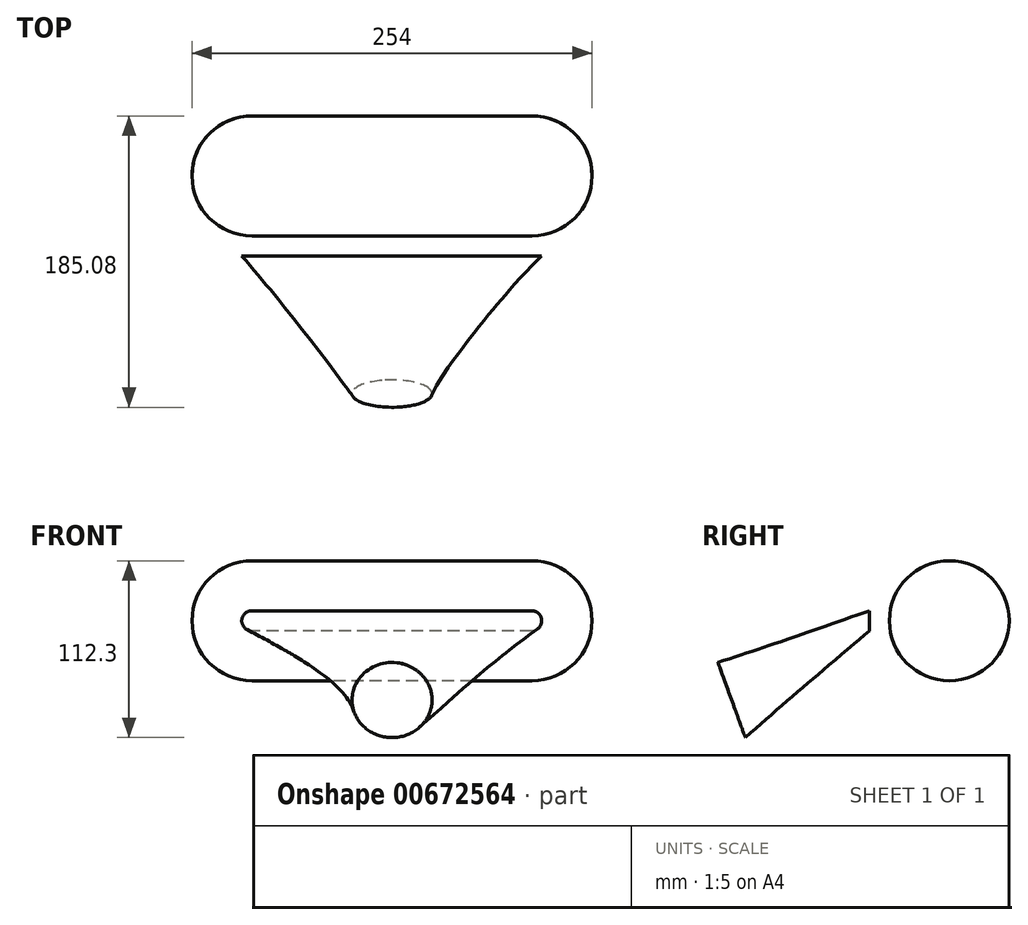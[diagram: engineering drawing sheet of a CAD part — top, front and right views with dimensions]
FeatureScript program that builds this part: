
annotation { "Feature Type Name" : "Feature", "Feature Type Description" : "" }
export const myFeature = defineFeature(function(context is Context, id is Id, definition is map)
    precondition{}
    {
        {
            var Q0;
            Q0=qCreatedBy(makeId("Top.planeOp"),FACE);
            var sketch = newSketch(context, id + "F0", { "sketchPlane" : qUnion([Q0])});
            skLineSegment(sketch, "E0", {"start": v(-127, 0) * mm, "end": v(127, 0) * mm});
            skArc(sketch, "E1", {"start": v(-127, 0) * mm, "mid": v(-115.84, 26.94) * mm, "end": v(-88.9, 38.1) * mm});
            skArc(sketch, "E2", {"start": v(127, 0) * mm, "mid": v(115.84, 26.94) * mm, "end": v(88.9, 38.1) * mm});
            skLineSegment(sketch, "E3", {"start": v(-88.9, 38.1) * mm, "end": v(88.9, 38.1) * mm});
            skSolve(sketch);
        }
        {
            var Q0;
            Q0=makeQuery(id+"F0.imprint","IMPRINT",FACE,{"disambiguationData":[TD([[makeQuery(id+"F0.imprint","IMPRINT",EDGE,{"derivedFrom":sQuery(id+"F0.wireOp",EDGE,"E0")}),1.0]])]});
            var Q1;
            Q1=sQuery(id+"F0.wireOp",EDGE,"E0");
            revolve(context, id + "F1", {"entities" : qUnion([Q0]), "axis" : qUnion([Q1]), "revolveType" : RevolveType.FULL});
        }
        {
            var Q0;
            Q0=qCreatedBy(makeId("Front.planeOp"),FACE);
            cPlane(context, id + "F2", {"entities" : qUnion([Q0]), "cplaneType" : CPlaneType.OFFSET, "offset" : 50.8 * mm, "width" : 152.4 * mm, "height" : 152.4 * mm});
        }
        {
            var Q0;
            Q0=qCreatedBy(id+"F2.planeOp",FACE);
            var sketch = newSketch(context, id + "F3", { "sketchPlane" : qUnion([Q0])});
            skLineSegment(sketch, "E4", {"start": v(-89.1, 6.35) * mm, "end": v(88.7, 6.35) * mm});
            skLineSegment(sketch, "E5", {"start": v(88.83, -6.35) * mm, "end": v(-88.97, -6.35) * mm});
            skArc(sketch, "E6", {"start": v(88.7, 6.35) * mm, "mid": v(95.05, 0.06) * mm, "end": v(88.83, -6.35) * mm});
            skArc(sketch, "E7", {"start": v(-89.1, 6.35) * mm, "mid": v(-95.45, -0.06) * mm, "end": v(-88.97, -6.35) * mm});
            skSolve(sketch);
        }
        {
            var Q0;
            Q0=qCreatedBy(makeId("Front.planeOp"),FACE);
            cPlane(context, id + "F4", {"entities" : qUnion([Q0]), "cplaneType" : CPlaneType.OFFSET, "offset" : 152.4 * mm, "width" : 152.4 * mm, "height" : 152.4 * mm});
        }
        {
            var Q0;
            Q0=sQuery(id+"F3.wireOp",EDGE,"E4");
            var Q1;
            Q1=makeQuery(id+"F3.imprint","IMPRINT",FACE,{"disambiguationData":[TD([[makeQuery(id+"F3.imprint","IMPRINT",EDGE,{"derivedFrom":sQuery(id+"F3.wireOp",EDGE,"E4")}),-1.0]])]});
            cPlane(context, id + "F5", {"entities" : qUnion([Q0, Q1]), "cplaneType" : CPlaneType.LINE_ANGLE, "offset" : 50.8 * mm, "angle" : 20 * degree, "width" : 152.4 * mm, "height" : 152.4 * mm});
        }
        {
            var Q0;
            Q0=qCreatedBy(id+"F5.planeOp",FACE);
            cPlane(context, id + "F6", {"entities" : qUnion([Q0]), "cplaneType" : CPlaneType.OFFSET, "offset" : 101.6 * mm, "oppositeDirection" : true, "width" : 152.4 * mm, "height" : 152.4 * mm});
        }
        {
            var Q0;
            Q0=qCreatedBy(id+"F6.planeOp",FACE);
            var sketch = newSketch(context, id + "F7", { "sketchPlane" : qUnion([Q0])});
            skCircle(sketch, "E8", {"center": v(0, 0) * mm, "radius": 25.4 * mm});
            skSolve(sketch);
        }
        {
            var Q0;
            Q0=makeQuery(id+"F7.imprint","IMPRINT",FACE,{"disambiguationData":[TD([[makeQuery(id+"F7.imprint","IMPRINT",EDGE,{"derivedFrom":sQuery(id+"F7.wireOp",EDGE,"E8")}),1.0]])]});
            var Q1;
            Q1=makeQuery(id+"F3.imprint","IMPRINT",FACE,{"disambiguationData":[TD([[makeQuery(id+"F3.imprint","IMPRINT",EDGE,{"derivedFrom":sQuery(id+"F3.wireOp",EDGE,"E4")}),-1.0]])]});
            loft(context, id + "F8", {"sheetProfilesArray" : [{ "sheetProfileEntities" : qUnion([Q0]) }, { "sheetProfileEntities" : qUnion([Q1]) }]});
        }
    });
